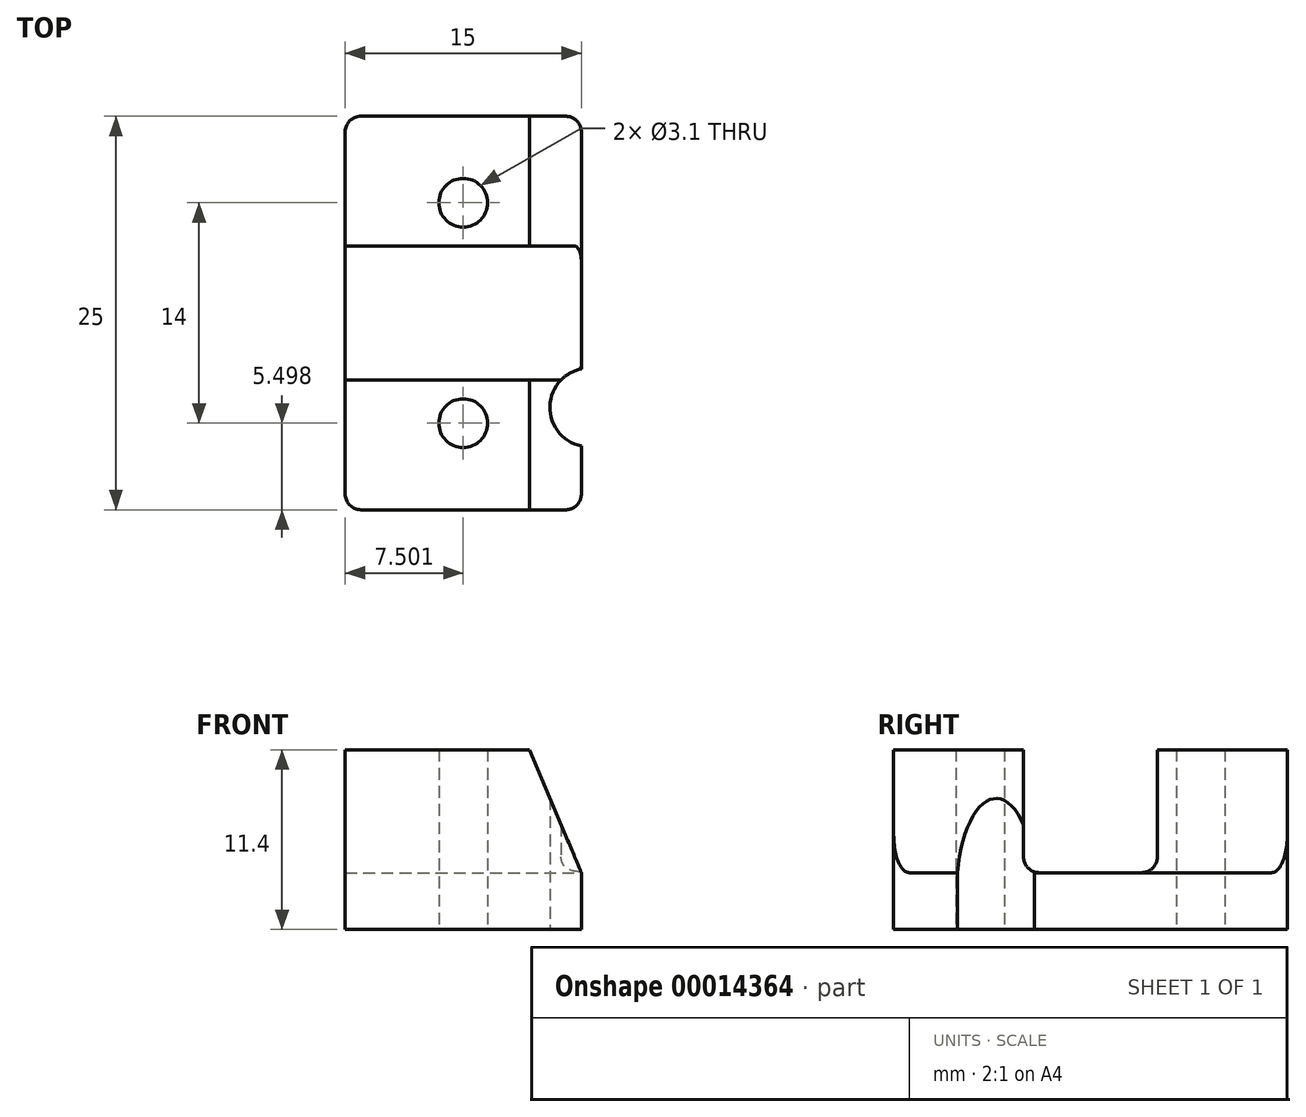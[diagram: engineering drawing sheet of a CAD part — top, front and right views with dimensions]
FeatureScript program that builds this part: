
annotation { "Feature Type Name" : "Feature", "Feature Type Description" : "" }
export const myFeature = defineFeature(function(context is Context, id is Id, definition is map)
    precondition{}
    {
        {
            var Q0;
            Q0=qCreatedBy(makeId("Top.planeOp"),FACE);
            var sketch = newSketch(context, id + "F0", { "sketchPlane" : qUnion([Q0])});
            skLineSegment(sketch, "E0.bottom", {"start": v(-21.78, 14.7) * mm, "end": v(-6.78, 14.7) * mm});
            skLineSegment(sketch, "E0.top", {"start": v(-21.78, -10.3) * mm, "end": v(-6.78, -10.3) * mm});
            skLineSegment(sketch, "E0.left", {"start": v(-21.78, 14.7) * mm, "end": v(-21.78, -10.3) * mm});
            skLineSegment(sketch, "E0.right", {"start": v(-6.78, 14.7) * mm, "end": v(-6.78, -10.3) * mm});
            skCircle(sketch, "E1", {"center": v(-14.28, 9.2) * mm, "radius": 1.55 * mm});
            skCircle(sketch, "E2", {"center": v(-14.28, -4.8) * mm, "radius": 1.55 * mm});
            skLineSegment(sketch, "E3", {"start": v(-21.78, 6.16) * mm, "end": v(-6.78, 6.16) * mm});
            skLineSegment(sketch, "E4", {"start": v(-21.78, -1.74) * mm, "end": v(-6.78, -1.74) * mm});
            skSolve(sketch);
        }
        {
            var Q0;
            Q0=qSketchRegion(id+"F0",true);
            extrude(context, id + "F1", {"entities" : qUnion([Q0]), "depth" : 11.4 * mm});
        }
        {
            var Q0;
            Q0=makeQuery(id+"F1.opExtrude","SWEPT_FACE",FACE,{"disambiguationData":[OSD([sQuery(id+"F0.wireOp",EDGE,"E0.right")])]});
            var sketch = newSketch(context, id + "F2", { "sketchPlane" : qUnion([Q0])});
            skLineSegment(sketch, "E5.bottom", {"start": v(-2.04, 11.4) * mm, "end": v(6.46, 11.4) * mm});
            skLineSegment(sketch, "E5.top", {"start": v(-2.04, 3.6) * mm, "end": v(6.46, 3.6) * mm});
            skLineSegment(sketch, "E5.left", {"start": v(-2.04, 11.4) * mm, "end": v(-2.04, 3.6) * mm});
            skLineSegment(sketch, "E5.right", {"start": v(6.46, 11.4) * mm, "end": v(6.46, 3.6) * mm});
            skSolve(sketch);
        }
        {
            var Q0;
            Q0=makeQuery(id+"F2.imprint","IMPRINT",FACE,{"disambiguationData":[TD([[makeQuery(id+"F2.imprint","IMPRINT",EDGE,{"derivedFrom":sQuery(id+"F2.wireOp",EDGE,"E5.bottom")}),1.0]])]});
            var Q1;
            Q1=makeQuery(id+"F1.opExtrude","SWEPT_FACE",FACE,{"disambiguationData":[OSD([sQuery(id+"F0.wireOp",EDGE,"E0.left")])]});
            extrude(context, id + "F3", {"entities" : qUnion([Q0]), "operationType" : NewBodyOperationType.REMOVE, "endBound" : BoundingType.UP_TO_SURFACE, "oppositeDirection" : true, "endBoundEntityFace" : qUnion([Q1]), "depth" : 25 * mm});
        }
        {
            var Q0;
            Q0=makeQuery(id+"F3.boolean.opBoolean","COPY",EDGE,{"derivedFrom":makeQuery(id+"F3.opExtrude","SWEPT_EDGE",EDGE,{"disambiguationData":[OSD([sQuery(id+"F2.wireOp",EDGE,"E5.top"),sQuery(id+"F2.wireOp",EDGE,"E5.left")])]})});
            var Q1;
            Q1=makeQuery(id+"F3.boolean.opBoolean","COPY",EDGE,{"derivedFrom":makeQuery(id+"F3.opExtrude","SWEPT_EDGE",EDGE,{"disambiguationData":[OSD([sQuery(id+"F2.wireOp",EDGE,"E5.top"),sQuery(id+"F2.wireOp",EDGE,"E5.right")])]})});
            fillet(context, id + "F4", {"entities" : qUnion([Q0, Q1]), "radius" : 1 * mm, "tangentPropagation" : true, "allowEdgeOverflow" : false});
        }
        {
            var Q0;
            Q0=makeQuery(id+"F1.opExtrude","SWEPT_FACE",FACE,{"disambiguationData":[OSD([sQuery(id+"F0.wireOp",EDGE,"E0.top")])]});
            var sketch = newSketch(context, id + "F5", { "sketchPlane" : qUnion([Q0])});
            skLineSegment(sketch, "E6", {"start": v(-10.08, 11.4) * mm, "end": v(-6.78, 3.6) * mm});
            skSolve(sketch);
        }
        {
            var Q0;
            Q0=qSketchRegion(id+"F5",true);
            var Q1;
            {var subQ2=sQuery(id+"F5.wireOp",EDGE,"E6");Q1=makeQuery(id+"F5.imprint","IMPRINT",FACE,{"disambiguationData":[TD([[makeQuery(id+"F5.imprint","IMPRINT",EDGE,{"derivedFrom":subQ2}),1.0]])]});}
            var Q2;
            Q2=makeQuery(id+"F1.opExtrude","SWEPT_FACE",FACE,{"disambiguationData":[OSD([sQuery(id+"F0.wireOp",EDGE,"E0.bottom")])]});
            extrude(context, id + "F6", {"entities" : qUnion([Q0, Q1]), "operationType" : NewBodyOperationType.REMOVE, "endBound" : BoundingType.UP_TO_SURFACE, "oppositeDirection" : true, "endBoundEntityFace" : qUnion([Q2]), "depth" : 25 * mm});
        }
        {
            var Q0;
            Q0=makeQuery(id+"F1.opExtrude","SWEPT_EDGE",EDGE,{"disambiguationData":[OSD([sQuery(id+"F0.wireOp",EDGE,"E0.top"),sQuery(id+"F0.wireOp",EDGE,"E0.right")])]});
            var Q1;
            Q1=makeQuery(id+"F1.opExtrude","SWEPT_EDGE",EDGE,{"disambiguationData":[OSD([sQuery(id+"F0.wireOp",EDGE,"E0.bottom"),sQuery(id+"F0.wireOp",EDGE,"E0.right")])]});
            var Q2;
            Q2=makeQuery(id+"F1.opExtrude","SWEPT_EDGE",EDGE,{"disambiguationData":[OSD([sQuery(id+"F0.wireOp",EDGE,"E0.top"),sQuery(id+"F0.wireOp",EDGE,"E0.left")])]});
            var Q3;
            Q3=makeQuery(id+"F1.opExtrude","SWEPT_EDGE",EDGE,{"disambiguationData":[OSD([sQuery(id+"F0.wireOp",EDGE,"E0.bottom"),sQuery(id+"F0.wireOp",EDGE,"E0.left")])]});
            fillet(context, id + "F7", {"entities" : qUnion([Q0, Q1, Q2, Q3]), "radius" : 1 * mm, "tangentPropagation" : true, "allowEdgeOverflow" : false});
        }
        {
            var Q0;
            {var subQ1=sQuery(id+"F0.wireOp",EDGE,"E3");Q0=makeQuery(id+"F0.imprint","IMPRINT",FACE,{"disambiguationData":[TD([[makeQuery(id+"F0.imprint","IMPRINT",EDGE,{"derivedFrom":subQ1}),-1.0]])]});}
            var sketch = newSketch(context, id + "F8", { "sketchPlane" : qUnion([Q0])});
            skCircle(sketch, "E7", {"center": v(-6.28, -3.8) * mm, "radius": 2.5 * mm});
            skSolve(sketch);
        }
        {
            var Q0;
            Q0=qSketchRegion(id+"F8",true);
            extrude(context, id + "F9", {"entities" : qUnion([Q0]), "operationType" : NewBodyOperationType.REMOVE, "depth" : 25 * mm});
        }
    });
